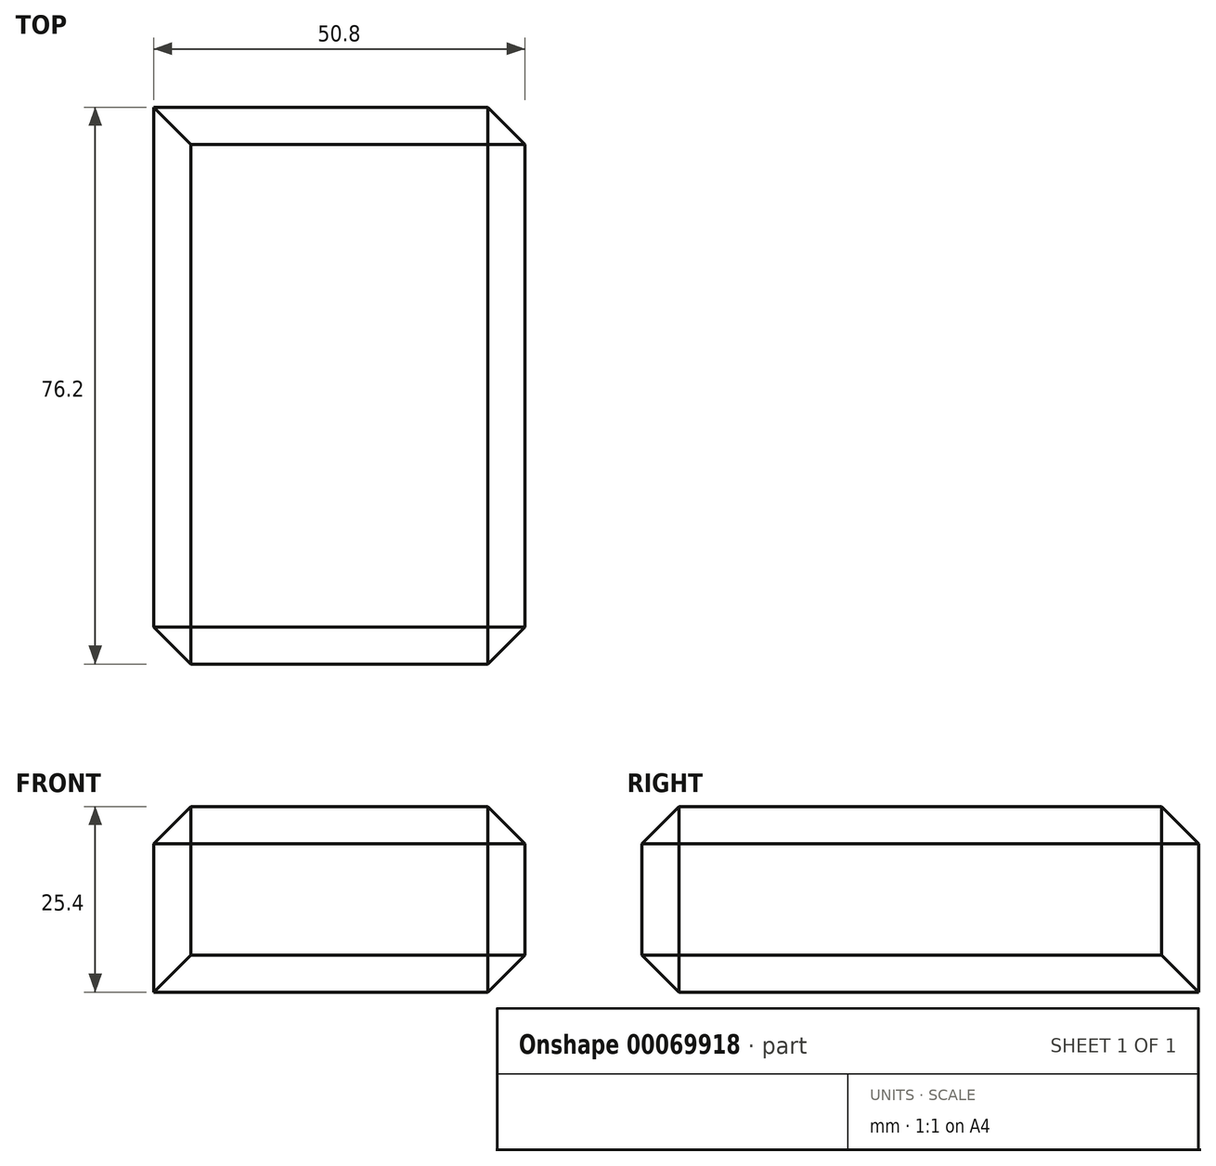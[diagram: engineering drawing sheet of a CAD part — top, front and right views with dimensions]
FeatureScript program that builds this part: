
annotation { "Feature Type Name" : "Feature", "Feature Type Description" : "" }
export const myFeature = defineFeature(function(context is Context, id is Id, definition is map)
    precondition{}
    {
        {
            var Q0;
            Q0=qCreatedBy(makeId("Top.planeOp"),FACE);
            var sketch = newSketch(context, id + "F0", { "sketchPlane" : qUnion([Q0])});
            skLineSegment(sketch, "E0.rect.bottom", {"start": v(25.4, 38.1) * mm, "end": v(-25.4, 38.1) * mm});
            skLineSegment(sketch, "E0.rect.top", {"start": v(25.4, -38.1) * mm, "end": v(-25.4, -38.1) * mm});
            skLineSegment(sketch, "E0.rect.left", {"start": v(25.4, 38.1) * mm, "end": v(25.4, -38.1) * mm});
            skLineSegment(sketch, "E0.rect.right", {"start": v(-25.4, 38.1) * mm, "end": v(-25.4, -38.1) * mm});
            skPoint(sketch, "E0.rect.middle", {"position": v(0, 0) * mm});
            skSolve(sketch);
        }
        {
            var Q0;
            Q0=makeQuery(id+"F0.imprint","IMPRINT",FACE,{"disambiguationData":[TD([[makeQuery(id+"F0.imprint","IMPRINT",EDGE,{"derivedFrom":sQuery(id+"F0.wireOp",EDGE,"E0.rect.bottom")}),1.0]])]});
            extrude(context, id + "F1", {"entities" : qUnion([Q0]), "depth" : 25.4 * mm});
        }
        {
            var Q0;
            Q0=makeQuery(id+"F1.opExtrude","CAP_FACE",FACE,{"disambiguationData":[OSD([sQuery(id+"F0.wireOp",EDGE,"E0.rect.bottom"),sQuery(id+"F0.wireOp",EDGE,"E0.rect.top"),sQuery(id+"F0.wireOp",EDGE,"E0.rect.left"),sQuery(id+"F0.wireOp",EDGE,"E0.rect.right")])],"isStart":false});
            var Q1;
            Q1=makeQuery(id+"F1.opExtrude","SWEPT_FACE",FACE,{"disambiguationData":[OSD([sQuery(id+"F0.wireOp",EDGE,"E0.rect.top")])]});
            var Q2;
            Q2=makeQuery(id+"F1.opExtrude","SWEPT_FACE",FACE,{"disambiguationData":[OSD([sQuery(id+"F0.wireOp",EDGE,"E0.rect.left")])]});
            chamfer(context, id + "F2", {"entities" : qUnion([Q0, Q1, Q2]), "width" : 5.08 * mm, "tangentPropagation" : true});
        }
    });
